# Revit family: Faucet-Valves_and_Controls-KOHLER-K-31141T
name_source: partatom
category: Plumbing Fixtures
units: mm (PartAtom-declared; Revit-internal decimal feet)

## family parameters
Cut with Voids When Loaded = No
Host = Face
OmniClass Number = 23.27.31.00
OmniClass Title = Valves
Part Type = Normal
Room Calculation Point = No
Round Connector Dimension = Use Diameter
Shared = No

## types (2) — shared parameters
ADA Compliant = No
Assembly Code = D2020
CW Connection = Yes
Cold Water Inlet = Cold Water Inlet
Date Modified = 02/28/2023
Default Elevation = 36"
Description = Double Handle Wall Outlet Basin Faucet Valve Core Type A
Finish = Kohler-Metal-Brass
Flow Rate = 0 GPM
HW Connection = Yes
Height = 2 1/16"
Hot Water Inlet = Hot Water Inlet
Length = 2 11/16"
Manufacturer = Kohler Co.
Master Format 2014 = 23 09 13.33
Master Format 2014 Name = Control Valves
Material = Brass Construction
Pressure = 0.80 psi
URL = http://www.kohler.com.cn
Vent Connection = No
Waste Connection = No
Waste Water Outlet = Waste Water Outlet
WaterSense Certified = No
Width = 11"

## per-type parameters (varying)
| type | Model | Product Documentation Link | Product Page URL | Type |
| NA-Brass | K-31141T-NA | https://files.kohler.com.cn | https://www.kohler.com.cn | 1 |
| DR, NA-Brass | K-31141T-DR-NA |  |  | 2 |

## geometry (parser evidence)
native form markers: Sweep x4
no freeform markers — native parametric forms only
